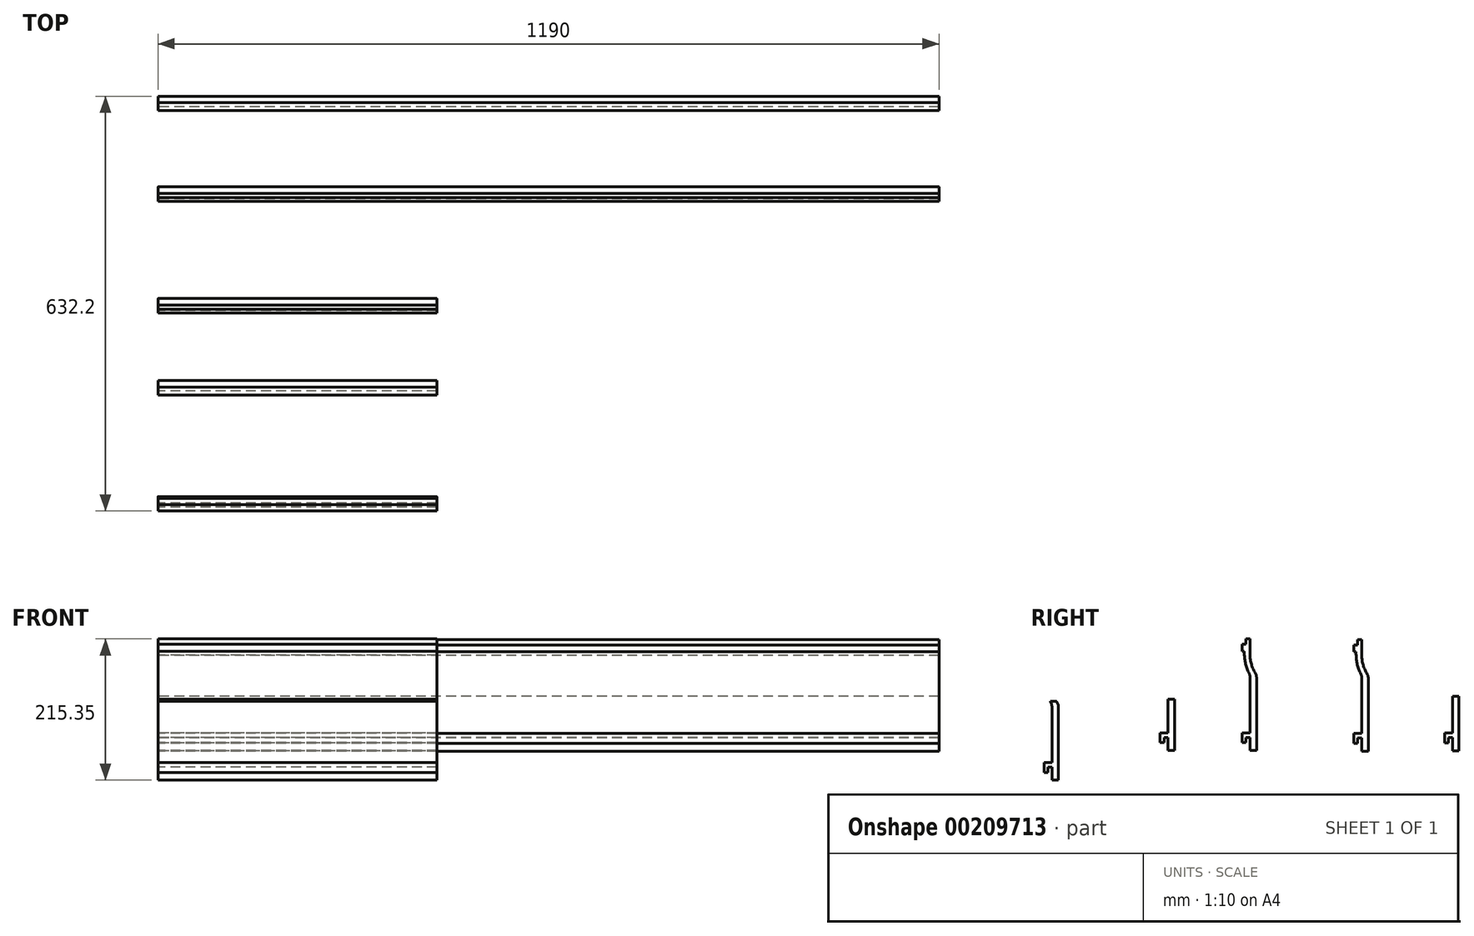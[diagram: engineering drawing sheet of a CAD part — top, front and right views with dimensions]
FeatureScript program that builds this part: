
annotation { "Feature Type Name" : "Feature", "Feature Type Description" : "" }
export const myFeature = defineFeature(function(context is Context, id is Id, definition is map)
    precondition{}
    {
        {
            var Q0;
            Q0=qCreatedBy(makeId("Right.planeOp"),FACE);
            var sketch = newSketch(context, id + "F0", { "sketchPlane" : qUnion([Q0]), "disableImprinting" : false});
            skLineSegment(sketch, "E0", {"start": v(0, 0) * mm, "end": v(0, 112.05) * mm});
            skLineSegment(sketch, "E1", {"start": v(0, 0) * mm, "end": v(-10, 0) * mm});
            skLineSegment(sketch, "E2", {"start": v(-10, 0) * mm, "end": v(-10, 20) * mm});
            skLineSegment(sketch, "E3", {"start": v(-10, 20) * mm, "end": v(-16, 20) * mm});
            skLineSegment(sketch, "E4", {"start": v(-16, 20) * mm, "end": v(-16, 12) * mm});
            skLineSegment(sketch, "E5", {"start": v(-16, 12) * mm, "end": v(-22, 12) * mm});
            skLineSegment(sketch, "E6", {"start": v(-22, 12) * mm, "end": v(-22, 26.9) * mm});
            skLineSegment(sketch, "E7", {"start": v(-22, 26.9) * mm, "end": v(-10, 26.9) * mm});
            skLineSegment(sketch, "E8", {"start": v(-10, 26.9) * mm, "end": v(-10, 112.71) * mm});
            skLineSegment(sketch, "E9", {"start": v(-16, 170) * mm, "end": v(-10, 170) * mm});
            skLineSegment(sketch, "E10", {"start": v(-18.43, 151.38) * mm, "end": v(-18.43, 147.58) * mm});
            skArc(sketch, "E11", {"start": v(-10, 145.68) * mm, "mid": v(-7.59, 130.93) * mm, "end": v(-1.48, 117.28) * mm});
            skArc(sketch, "E12.0", {"start": v(-18.43, 147.58) * mm, "mid": v(-16.57, 132) * mm, "end": v(-11.1, 117.28) * mm});
            skLineSegment(sketch, "E13.trimOffspring", {"start": v(-10, 145.68) * mm, "end": v(-10, 170) * mm});
            skLineSegment(sketch, "E14", {"start": v(-16, 170) * mm, "end": v(-16, 162) * mm});
            skLineSegment(sketch, "E15", {"start": v(-16, 162) * mm, "end": v(-22, 162) * mm});
            skLineSegment(sketch, "E16", {"start": v(-22, 162) * mm, "end": v(-22, 151.38) * mm});
            skLineSegment(sketch, "E17", {"start": v(-22, 151.38) * mm, "end": v(-18.43, 151.38) * mm});
            skPoint(sketch, "E18.visualSharp", {"position": v(0, 115) * mm});
            skArc(sketch, "E18.filletArc", {"start": v(0, 112.05) * mm, "mid": v(-0.38, 114.77) * mm, "end": v(-1.48, 117.28) * mm});
            skPoint(sketch, "E19.visualSharp", {"position": v(-10, 115.22) * mm});
            skArc(sketch, "E19.filletArc", {"start": v(-10, 112.71) * mm, "mid": v(-10.28, 115.06) * mm, "end": v(-11.1, 117.28) * mm});
            skSolve(sketch);
        }
        {
            var Q0;
            Q0 = qSketchRegion(id + "F0", true);
            extrude(context, id + "F1", {"entities" : qUnion([Q0]), "offsetDistance" : 25 * mm, "depth" : 1190 * mm});
        }
        {
            var Q0;
            Q0=qCreatedBy(makeId("Right.planeOp"),FACE);
            var sketch = newSketch(context, id + "F2", { "sketchPlane" : qUnion([Q0]), "disableImprinting" : false});
            skLineSegment(sketch, "E20", {"start": v(-170.22, 1.04) * mm, "end": v(-170.22, 113.1) * mm});
            skLineSegment(sketch, "E21", {"start": v(-170.22, 1.04) * mm, "end": v(-180.22, 1.04) * mm});
            skLineSegment(sketch, "E22", {"start": v(-180.22, 1.04) * mm, "end": v(-180.22, 21.04) * mm});
            skLineSegment(sketch, "E23", {"start": v(-180.22, 21.04) * mm, "end": v(-186.22, 21.04) * mm});
            skLineSegment(sketch, "E24", {"start": v(-186.22, 21.04) * mm, "end": v(-186.22, 13.04) * mm});
            skLineSegment(sketch, "E25", {"start": v(-186.22, 13.04) * mm, "end": v(-192.22, 13.04) * mm});
            skLineSegment(sketch, "E26", {"start": v(-192.22, 13.04) * mm, "end": v(-192.22, 27.94) * mm});
            skLineSegment(sketch, "E27", {"start": v(-192.22, 27.94) * mm, "end": v(-180.22, 27.94) * mm});
            skLineSegment(sketch, "E28", {"start": v(-180.22, 27.94) * mm, "end": v(-180.22, 113.75) * mm});
            skLineSegment(sketch, "E29", {"start": v(-186.22, 171.04) * mm, "end": v(-180.22, 171.04) * mm});
            skLineSegment(sketch, "E30", {"start": v(-188.65, 152.42) * mm, "end": v(-188.65, 148.62) * mm});
            skArc(sketch, "E31", {"start": v(-180.22, 146.72) * mm, "mid": v(-177.8, 131.97) * mm, "end": v(-171.7, 118.32) * mm});
            skArc(sketch, "E32.0", {"start": v(-188.65, 148.62) * mm, "mid": v(-186.8, 133.03) * mm, "end": v(-181.32, 118.32) * mm});
            skLineSegment(sketch, "E33.trimOffspring", {"start": v(-180.22, 146.72) * mm, "end": v(-180.22, 171.04) * mm});
            skLineSegment(sketch, "E34", {"start": v(-186.22, 171.04) * mm, "end": v(-186.22, 163.04) * mm});
            skLineSegment(sketch, "E35", {"start": v(-186.22, 163.04) * mm, "end": v(-192.22, 163.04) * mm});
            skLineSegment(sketch, "E36", {"start": v(-192.22, 163.04) * mm, "end": v(-192.22, 152.42) * mm});
            skLineSegment(sketch, "E37", {"start": v(-192.22, 152.42) * mm, "end": v(-188.65, 152.42) * mm});
            skPoint(sketch, "E38.visualSharp", {"position": v(-170.22, 116.04) * mm});
            skArc(sketch, "E38.filletArc", {"start": v(-170.22, 113.1) * mm, "mid": v(-170.6, 115.81) * mm, "end": v(-171.7, 118.32) * mm});
            skPoint(sketch, "E39.visualSharp", {"position": v(-180.22, 116.26) * mm});
            skArc(sketch, "E39.filletArc", {"start": v(-180.22, 113.75) * mm, "mid": v(-180.5, 116.1) * mm, "end": v(-181.32, 118.32) * mm});
            skLineSegment(sketch, "E40", {"start": v(-295.05, 1.04) * mm, "end": v(-295.05, 79.04) * mm});
            skLineSegment(sketch, "E41", {"start": v(-295.05, 1.04) * mm, "end": v(-305.05, 1.04) * mm});
            skLineSegment(sketch, "E42", {"start": v(-305.05, 1.04) * mm, "end": v(-305.05, 21.04) * mm});
            skLineSegment(sketch, "E43", {"start": v(-305.05, 21.04) * mm, "end": v(-311.05, 21.04) * mm});
            skLineSegment(sketch, "E44", {"start": v(-311.05, 21.04) * mm, "end": v(-311.05, 13.04) * mm});
            skLineSegment(sketch, "E45", {"start": v(-311.05, 13.04) * mm, "end": v(-317.05, 13.04) * mm});
            skLineSegment(sketch, "E46", {"start": v(-317.05, 13.04) * mm, "end": v(-317.05, 27.94) * mm});
            skLineSegment(sketch, "E47", {"start": v(-317.05, 27.94) * mm, "end": v(-305.05, 27.94) * mm});
            skLineSegment(sketch, "E48", {"start": v(-305.05, 27.94) * mm, "end": v(-305.05, 79.04) * mm});
            skLineSegment(sketch, "E49", {"start": v(-311.05, 171.04) * mm, "end": v(-305.05, 171.04) * mm, "construction": true});
            skLineSegment(sketch, "E50", {"start": v(-313.49, 152.42) * mm, "end": v(-313.49, 148.62) * mm, "construction": true});
            skArc(sketch, "E51", {"start": v(-305.05, 146.72) * mm, "mid": v(-302.76, 132.37) * mm, "end": v(-296.96, 119.04) * mm, "construction": true});
            skArc(sketch, "E52.0", {"start": v(-313.49, 148.62) * mm, "mid": v(-311.72, 133.43) * mm, "end": v(-306.52, 119.04) * mm, "construction": true});
            skLineSegment(sketch, "E53.trimOffspring", {"start": v(-305.05, 146.72) * mm, "end": v(-305.05, 171.04) * mm, "construction": true});
            skLineSegment(sketch, "E54", {"start": v(-311.05, 171.04) * mm, "end": v(-311.05, 163.04) * mm, "construction": true});
            skLineSegment(sketch, "E55", {"start": v(-311.05, 163.04) * mm, "end": v(-317.05, 163.04) * mm, "construction": true});
            skLineSegment(sketch, "E56", {"start": v(-317.05, 163.04) * mm, "end": v(-317.05, 152.42) * mm, "construction": true});
            skLineSegment(sketch, "E57", {"start": v(-317.05, 152.42) * mm, "end": v(-313.49, 152.42) * mm, "construction": true});
            skPoint(sketch, "E58.visualSharp", {"position": v(-295.05, 116.04) * mm});
            skArc(sketch, "E58.filletArc", {"start": v(-295.05, 113.1) * mm, "mid": v(-295.43, 115.81) * mm, "end": v(-296.53, 118.32) * mm, "construction": true});
            skPoint(sketch, "E59.visualSharp", {"position": v(-305.05, 116.26) * mm});
            skArc(sketch, "E59.filletArc", {"start": v(-305.05, 113.75) * mm, "mid": v(-305.33, 116.1) * mm, "end": v(-306.16, 118.32) * mm, "construction": true});
            skLineSegment(sketch, "E60", {"start": v(-296.96, 119.04) * mm, "end": v(-306.52, 119.04) * mm, "construction": true});
            skArc(sketch, "E61", {"start": v(-296.96, 119.04) * mm, "mid": v(-296.75, 118.68) * mm, "end": v(-296.53, 118.32) * mm, "construction": true});
            skArc(sketch, "E62", {"start": v(-306.52, 119.04) * mm, "mid": v(-306.34, 118.68) * mm, "end": v(-306.16, 118.32) * mm, "construction": true});
            skLineSegment(sketch, "E63", {"start": v(-289.32, 79.04) * mm, "end": v(-319.24, 79.04) * mm});
            skLineSegment(sketch, "E64", {"start": v(-295.05, 79.04) * mm, "end": v(-295.05, 113.1) * mm, "construction": true});
            skLineSegment(sketch, "E65", {"start": v(-305.05, 79.04) * mm, "end": v(-305.05, 113.75) * mm, "construction": true});
            skLineSegment(sketch, "E66", {"start": v(-471.96, -44.31) * mm, "end": v(-471.96, 67.74) * mm});
            skLineSegment(sketch, "E67", {"start": v(-471.96, -44.31) * mm, "end": v(-481.96, -44.31) * mm});
            skLineSegment(sketch, "E68", {"start": v(-481.96, -44.31) * mm, "end": v(-481.96, -24.31) * mm});
            skLineSegment(sketch, "E69", {"start": v(-481.96, -24.31) * mm, "end": v(-487.96, -24.31) * mm});
            skLineSegment(sketch, "E70", {"start": v(-487.96, -24.31) * mm, "end": v(-487.96, -32.31) * mm});
            skLineSegment(sketch, "E71", {"start": v(-487.96, -32.31) * mm, "end": v(-493.96, -32.31) * mm});
            skLineSegment(sketch, "E72", {"start": v(-493.96, -32.31) * mm, "end": v(-493.96, -17.42) * mm});
            skLineSegment(sketch, "E73", {"start": v(-493.96, -17.42) * mm, "end": v(-481.96, -17.42) * mm});
            skLineSegment(sketch, "E74", {"start": v(-481.96, -17.42) * mm, "end": v(-481.96, 68.4) * mm});
            skLineSegment(sketch, "E75", {"start": v(-487.96, 125.69) * mm, "end": v(-481.96, 125.69) * mm, "construction": true});
            skLineSegment(sketch, "E76", {"start": v(-490.4, 107.07) * mm, "end": v(-490.4, 103.27) * mm, "construction": true});
            skArc(sketch, "E77", {"start": v(-481.96, 101.36) * mm, "mid": v(-479.98, 88.12) * mm, "end": v(-475, 75.69) * mm, "construction": true});
            skArc(sketch, "E78.0", {"start": v(-490.4, 103.27) * mm, "mid": v(-488.87, 89.15) * mm, "end": v(-484.39, 75.69) * mm, "construction": true});
            skLineSegment(sketch, "E79.trimOffspring", {"start": v(-481.96, 101.36) * mm, "end": v(-481.96, 125.69) * mm, "construction": true});
            skLineSegment(sketch, "E80", {"start": v(-487.96, 125.69) * mm, "end": v(-487.96, 117.69) * mm, "construction": true});
            skLineSegment(sketch, "E81", {"start": v(-487.96, 117.69) * mm, "end": v(-493.96, 117.69) * mm, "construction": true});
            skLineSegment(sketch, "E82", {"start": v(-493.96, 117.69) * mm, "end": v(-493.96, 107.07) * mm, "construction": true});
            skLineSegment(sketch, "E83", {"start": v(-493.96, 107.07) * mm, "end": v(-490.4, 107.07) * mm, "construction": true});
            skPoint(sketch, "E84.visualSharp", {"position": v(-471.96, 70.69) * mm});
            skArc(sketch, "E84.filletArc", {"start": v(-471.96, 67.74) * mm, "mid": v(-472.34, 70.46) * mm, "end": v(-473.44, 72.97) * mm});
            skPoint(sketch, "E85.visualSharp", {"position": v(-481.96, 70.9) * mm});
            skArc(sketch, "E85.filletArc", {"start": v(-481.96, 68.4) * mm, "mid": v(-482.24, 70.75) * mm, "end": v(-483.07, 72.96) * mm});
            skLineSegment(sketch, "E86", {"start": v(-484.39, 75.69) * mm, "end": v(-475, 75.69) * mm});
            skArc(sketch, "E87", {"start": v(-475, 75.69) * mm, "mid": v(-474.24, 74.32) * mm, "end": v(-473.44, 72.97) * mm});
            skArc(sketch, "E88", {"start": v(-484.39, 75.69) * mm, "mid": v(-483.74, 74.32) * mm, "end": v(-483.07, 72.96) * mm});
            skSolve(sketch);
        }
        {
            var Q0;
            Q0 = qSketchRegion(id + "F2", true);
            extrude(context, id + "F3", {"entities" : qUnion([Q0]), "flatOperationType" : FlatOperationType.REMOVE, "offsetDistance" : 25 * mm, "depth" : 425 * mm, "domain" : OperationDomain.MODEL});
        }
        {
            var Q0;
            Q0=qCreatedBy(makeId("Right.planeOp"),FACE);
            var sketch = newSketch(context, id + "F4", { "sketchPlane" : qUnion([Q0])});
            skLineSegment(sketch, "E89", {"start": v(138.24, 0.6) * mm, "end": v(138.24, 83.6) * mm});
            skLineSegment(sketch, "E90", {"start": v(138.24, 0.6) * mm, "end": v(128.24, 0.6) * mm});
            skLineSegment(sketch, "E91", {"start": v(128.24, 0.6) * mm, "end": v(128.24, 20.6) * mm});
            skLineSegment(sketch, "E92", {"start": v(128.24, 20.6) * mm, "end": v(122.24, 20.6) * mm});
            skLineSegment(sketch, "E93", {"start": v(122.24, 20.6) * mm, "end": v(122.24, 12.6) * mm});
            skLineSegment(sketch, "E94", {"start": v(122.24, 12.6) * mm, "end": v(116.24, 12.6) * mm});
            skLineSegment(sketch, "E95", {"start": v(116.24, 12.6) * mm, "end": v(116.24, 27.5) * mm});
            skLineSegment(sketch, "E96", {"start": v(116.24, 27.5) * mm, "end": v(128.24, 27.5) * mm});
            skLineSegment(sketch, "E97", {"start": v(128.24, 27.5) * mm, "end": v(128.24, 83.6) * mm});
            skLineSegment(sketch, "E98", {"start": v(128.24, 104.6) * mm, "end": v(138.24, 104.6) * mm, "construction": true});
            skLineSegment(sketch, "E99.top", {"start": v(138.24, 83.6) * mm, "end": v(128.24, 83.6) * mm});
            skLineSegment(sketch, "E100", {"start": v(138.24, 83.6) * mm, "end": v(138.24, 104.6) * mm, "construction": true});
            skLineSegment(sketch, "E101", {"start": v(128.24, 83.6) * mm, "end": v(128.24, 104.6) * mm, "construction": true});
            skSolve(sketch);
        }
        {
            var Q0;
            Q0 = qSketchRegion(id + "F4", true);
            extrude(context, id + "F5", {"entities" : qUnion([Q0]), "depth" : 1190 * mm, "offsetDistance" : 25 * mm});
        }
    });
